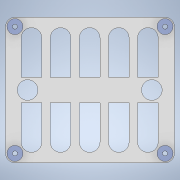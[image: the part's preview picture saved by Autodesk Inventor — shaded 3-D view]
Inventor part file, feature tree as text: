
AUTODESK INVENTOR PART (.ipt)
format: ipt  version: 2022 (Build 260153000, 153)  size: 252,928 bytes
history: native  units: mm
features: extrude x5, sketch x5, plane x2, hole x1
ambient origin geometry x8: Origin, YZ Plane, XZ Plane, XY Plane, X Axis, Y Axis, Z Axis, Center Point
bodies: Solid1 (feature_tree)
feature tree (13):
  extrude  "Extrusion1"  Depth=6.2mm
  extrude  "Extrusion2"  Depth=6.2mm
  extrude  "Extrusion3"  Depth=58.0mm
  hole  "Hole1"  [1 undecoded]
  sketch  "Sketch7"  dims[d16=2.0mm d17=0.0mm d18=7.25mm d19=7.25mm d20=7.25mm d21=7.25mm d22=2.0mm d23=0.0mm d27=8.0mm d28=8.0mm d29=8.0mm d30=8.0mm d31=10.0mm d32=10.0mm d33=50.0mm d35=11.25mm d36=10.0mm d38=10.0mm d40=2.0mm d41=0.0mm d42=2.0mm d43=6.0mm d44=4.0mm d45=2.0mm d46=90.0deg d47=8.0mm d48=20.594885mm d49=8.0mm d50=8.0mm d51=48.0mm d52=8.5mm d55=10.0mm d56=5.0mm d57=10.0mm d58=0.0mm d59=10.0mm d60=0.0mm d61=0.5mm d62=0.872665mm]
  plane  "Work Plane2"
  extrude  "Extrusion5"  Depth=10.0mm
  plane  "Work Plane1"
  extrude  "Extrusion6"  Depth=10.0mm
  sketch  "Sketch1"  dims[d4=6.2mm d5=6.2mm]
  sketch  "Sketch3"  dims[d6=6.2mm d7=6.2mm]
  sketch  "Sketch5"  dims[d12=58.0mm d13=58.0mm]
  sketch  "Sketch6"  dims[d14=49.0mm d15=49.0mm]
note: 1 required parameter value undecoded (feature->parameter linkage not recoverable at this tier; creation-order binding heuristic only, values carry confidence <= 0.55)
